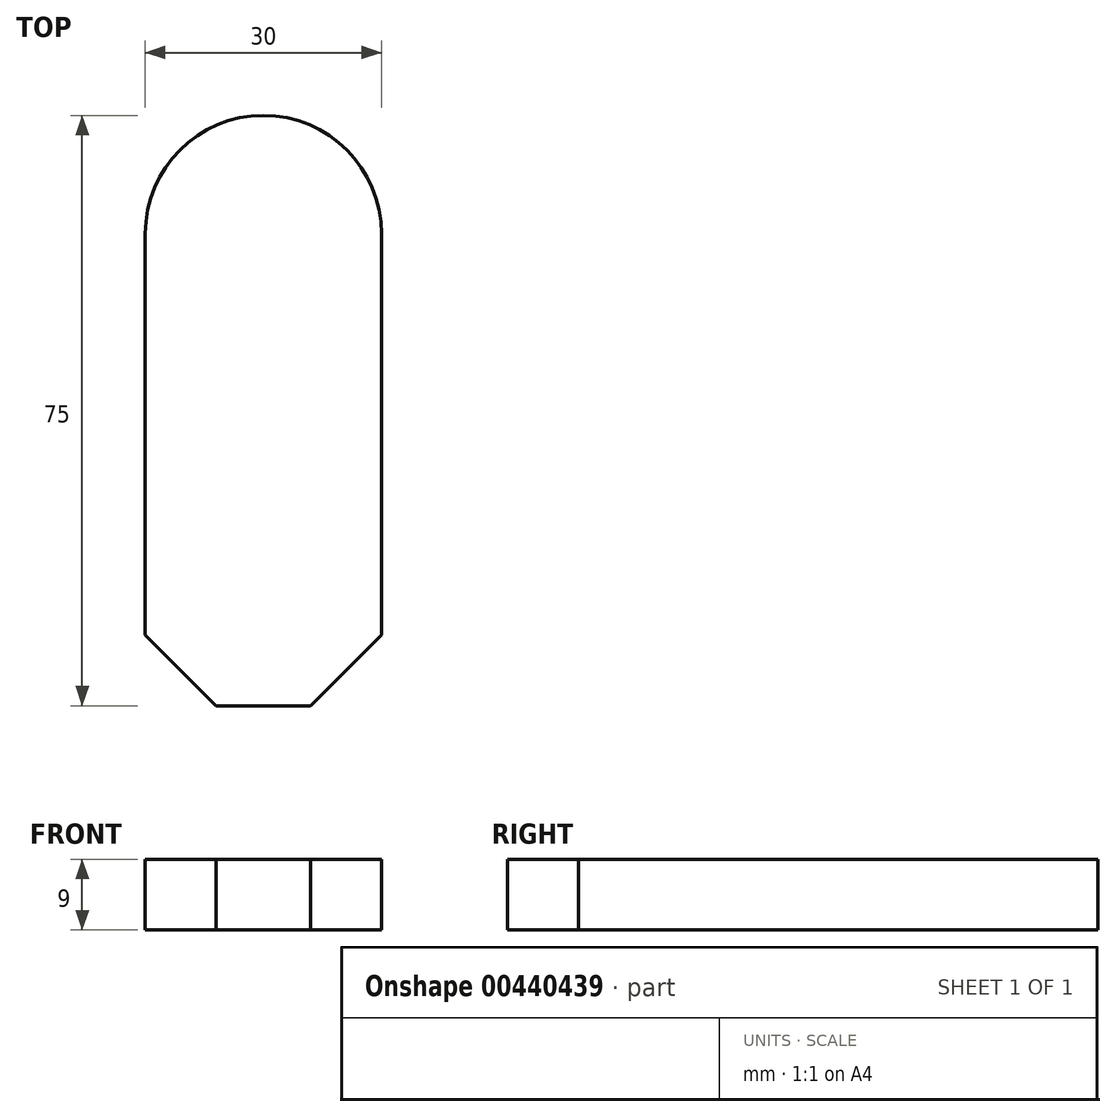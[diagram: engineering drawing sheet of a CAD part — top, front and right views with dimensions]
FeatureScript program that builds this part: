
annotation { "Feature Type Name" : "Feature", "Feature Type Description" : "" }
export const myFeature = defineFeature(function(context is Context, id is Id, definition is map)
    precondition{}
    {
        {
            var Q0;
            Q0=qCreatedBy(makeId("Top.planeOp"),FACE);
            var sketch = newSketch(context, id + "F0", { "sketchPlane" : qUnion([Q0])});
            skLineSegment(sketch, "E0", {"start": v(15, 0) * mm, "end": v(15, -51) * mm});
            skLineSegment(sketch, "E1", {"start": v(-15, -51) * mm, "end": v(-15, 0) * mm});
            skArc(sketch, "E2", {"start": v(15, 0) * mm, "mid": v(0, 15) * mm, "end": v(-15, 0) * mm});
            skLineSegment(sketch, "E3", {"start": v(-15, -51) * mm, "end": v(-6, -60) * mm});
            skLineSegment(sketch, "E4", {"start": v(6, -60) * mm, "end": v(15, -51) * mm});
            skLineSegment(sketch, "E5", {"start": v(-6, -60) * mm, "end": v(6, -60) * mm});
            skSolve(sketch);
        }
        {
            var Q0;
            Q0=makeQuery(id+"F0.imprint","IMPRINT",FACE,{"disambiguationData":[TD([[makeQuery(id+"F0.imprint","IMPRINT",EDGE,{"derivedFrom":sQuery(id+"F0.wireOp",EDGE,"E0")}),-1.0]])]});
            extrude(context, id + "F1", {"entities" : qUnion([Q0]), "depth" : 9 * mm});
        }
    });
